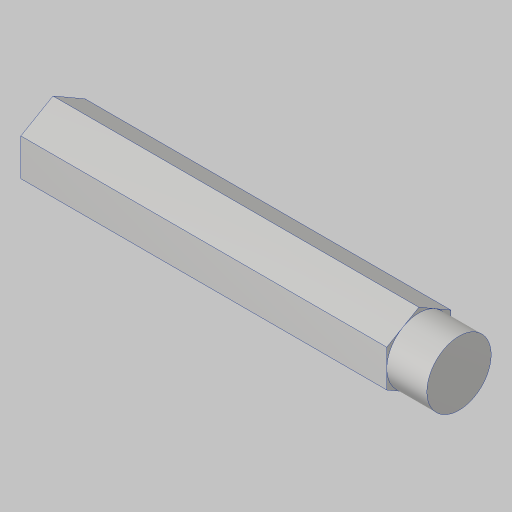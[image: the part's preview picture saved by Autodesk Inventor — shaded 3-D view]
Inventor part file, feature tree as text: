
AUTODESK INVENTOR PART (.ipt)
format: ipt  version: 2023.5 (Build 275446000, 446)  size: 124,928 bytes
history: native  units: in
note: dims shown in document units (in); Inventor stores cm internally (conversion verified against a paired STEP export)
features: sketch x3, extrude x2, hole x1, projected_geometry x1
ambient origin geometry x8: Origin, YZ Plane, XZ Plane, XY Plane, X Axis, Y Axis, Z Axis, Center Point
bodies: Solid1 (feature_tree)
feature tree (7):
  extrude  "Extrusion1"  Depth=3.163in TaperAngle=0.0deg
  extrude  "Extrusion2"  Depth=0.3125in TaperAngle=0.0deg
  hole  "Hole1"  [1 undecoded]
  sketch  "Sketch1"  dims[d0=0.5in d1=3.163in d2=0.0in]
  sketch  "Sketch2"  dims[d3=0.5in d4=0.3125in d5=0.0in]
  projected_geometry  "Projected Loop1"
  sketch  "Sketch4"  dims[d9=0.156in d10=0.38in d11=0.385in d12=0.25in d13=0.5635in d14=0.536in d15=0.8108in]
note: 1 required parameter value undecoded (feature->parameter linkage not recoverable at this tier; creation-order binding heuristic only, values carry confidence <= 0.55)
